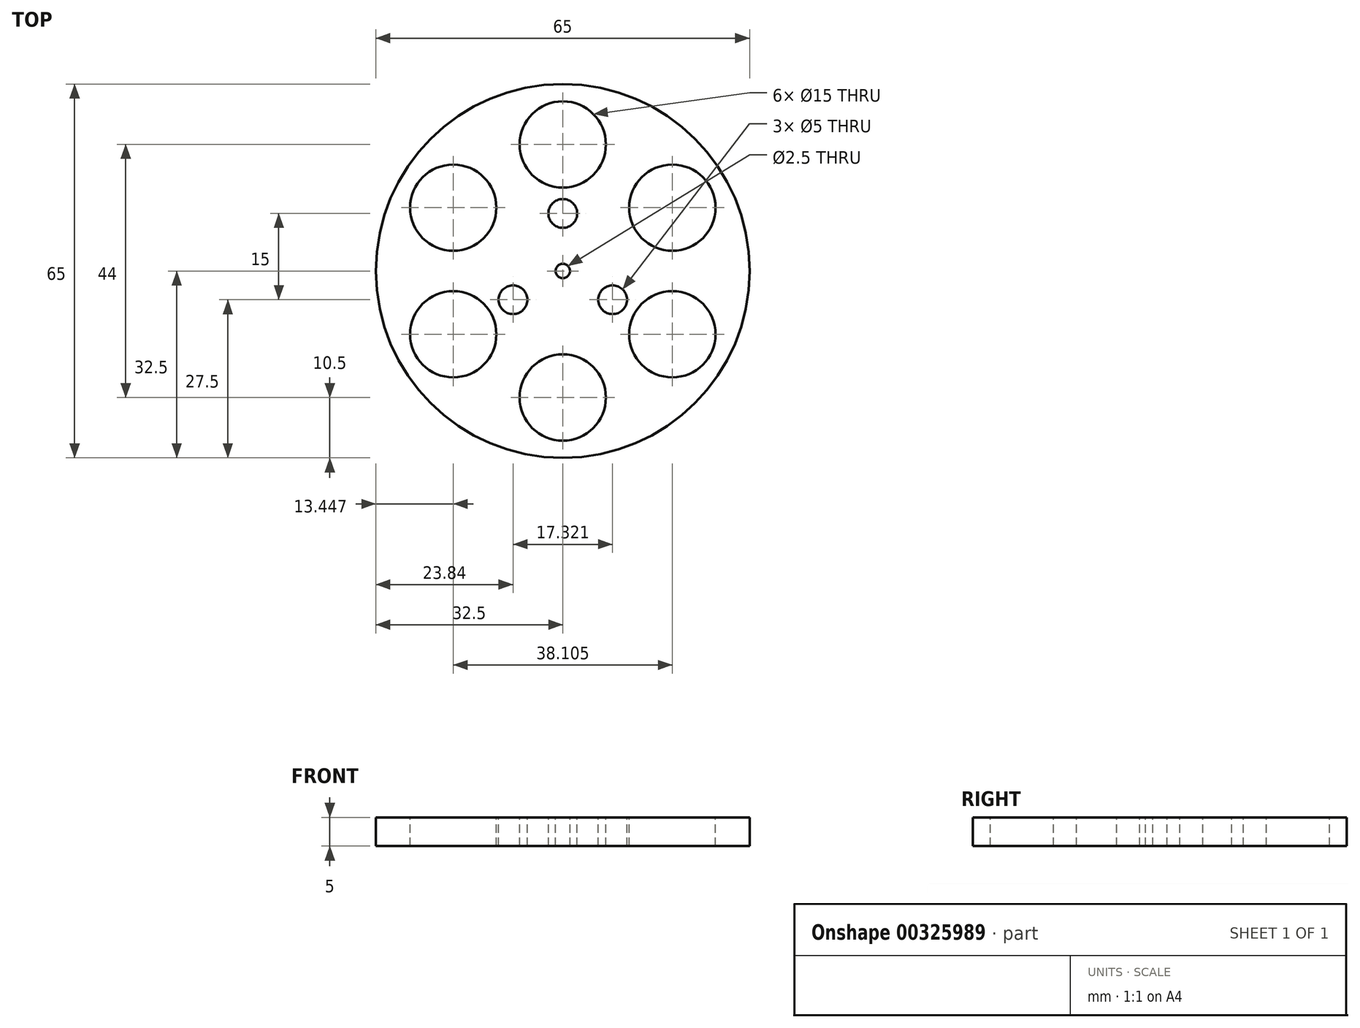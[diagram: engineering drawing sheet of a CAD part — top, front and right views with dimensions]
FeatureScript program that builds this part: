
annotation { "Feature Type Name" : "Feature", "Feature Type Description" : "" }
export const myFeature = defineFeature(function(context is Context, id is Id, definition is map)
    precondition{}
    {
        {
            var Q0;
            Q0=qCreatedBy(makeId("Top.planeOp"),FACE);
            var sketch = newSketch(context, id + "F0", { "sketchPlane" : qUnion([Q0])});
            skCircle(sketch, "E0", {"center": v(0, 0) * mm, "radius": 32.5 * mm});
            skLineSegment(sketch, "E1", {"start": v(0, 0) * mm, "end": v(0, 22) * mm});
            skLineSegment(sketch, "E2.1.0", {"start": v(0, 0) * mm, "end": v(19.05, 11) * mm});
            skLineSegment(sketch, "E2.2.0", {"start": v(0, 0) * mm, "end": v(19.05, -11) * mm});
            skLineSegment(sketch, "E2.3.0", {"start": v(0, 0) * mm, "end": v(0, -22) * mm});
            skLineSegment(sketch, "E2.4.0", {"start": v(0, 0) * mm, "end": v(-19.05, -11) * mm});
            skLineSegment(sketch, "E2.5.0", {"start": v(0, 0) * mm, "end": v(-19.05, 11) * mm});
            skLineSegment(sketch, "E2.anchor1", {"start": v(0, 0) * mm, "end": v(0, 22) * mm, "construction": true});
            skLineSegment(sketch, "E2.anchor2", {"start": v(0, 0) * mm, "end": v(-19.05, 11) * mm, "construction": true});
            skPoint(sketch, "E3", {"position": v(0, 10) * mm});
            skPoint(sketch, "E4.1.0", {"position": v(-8.66, -5) * mm});
            skPoint(sketch, "E4.2.0", {"position": v(8.66, -5) * mm});
            skSolve(sketch);
        }
        {
            var Q0;
            Q0=makeQuery(id+"F0.imprint","IMPRINT",FACE,{"disambiguationData":[TD([[makeQuery(id+"F0.imprint","IMPRINT",EDGE,{"derivedFrom":sQuery(id+"F0.wireOp",EDGE,"E0")}),1.0]])]});
            extrude(context, id + "F1", {"entities" : qUnion([Q0]), "depth" : 5 * mm, "offsetDistance" : 25 * mm});
        }
        {
            var Q0;
            Q0=sQuery(id+"F0.wireOp",VERTEX,"E2.1.0.end");
            var Q1;
            Q1=sQuery(id+"F0.wireOp",VERTEX,"E1.end");
            var Q2;
            Q2=sQuery(id+"F0.wireOp",VERTEX,"E2.5.0.end");
            var Q3;
            Q3=sQuery(id+"F0.wireOp",VERTEX,"E2.4.0.end");
            var Q4;
            Q4=sQuery(id+"F0.wireOp",VERTEX,"E2.3.0.end");
            var Q5;
            Q5=sQuery(id+"F0.wireOp",VERTEX,"E2.2.0.end");
            var Q6;
            Q6=makeQuery(id+"F1.opExtrude","SWEPT_BODY",BODY,{"disambiguationData":[OSD([sQuery(id+"F0.wireOp",EDGE,"E0")])]});
            hole(context, id + "F2", {"style" : HoleStyle.SIMPLE, "endStyle" : HoleEndStyle.THROUGH, "oppositeDirection" : true, "holeDiameter" : 15 * mm, "majorDiameter" : 5 * mm, "tappedDepth" : 12 * mm, "tapClearance" : 3, "locations" : qUnion([Q0, Q1, Q2, Q3, Q4, Q5]), "scope" : qUnion([Q6]), "startStyle" : HoleStartStyle.PART});
        }
        {
            var Q0;
            Q0=sQuery(id+"F0.wireOp",VERTEX,"E4.1.0");
            var Q1;
            Q1=sQuery(id+"F0.wireOp",VERTEX,"E3");
            var Q2;
            Q2=sQuery(id+"F0.wireOp",VERTEX,"E4.2.0");
            var Q3;
            Q3=makeQuery(id+"F1.opExtrude","SWEPT_BODY",BODY,{"disambiguationData":[OSD([sQuery(id+"F0.wireOp",EDGE,"E0")])]});
            hole(context, id + "F3", {"style" : HoleStyle.SIMPLE, "endStyle" : HoleEndStyle.THROUGH, "oppositeDirection" : true, "holeDiameter" : 5 * mm, "majorDiameter" : 5 * mm, "tappedDepth" : 12 * mm, "tapClearance" : 3, "locations" : qUnion([Q0, Q1, Q2]), "scope" : qUnion([Q3]), "startStyle" : HoleStartStyle.PART});
        }
        {
            var Q0;
            Q0=sQuery(id+"F0.wireOp",VERTEX,"E0.center");
            var Q1;
            Q1=makeQuery(id+"F1.opExtrude","SWEPT_BODY",BODY,{"disambiguationData":[OSD([sQuery(id+"F0.wireOp",EDGE,"E0")])]});
            hole(context, id + "F4", {"style" : HoleStyle.SIMPLE, "endStyle" : HoleEndStyle.BLIND, "oppositeDirection" : true, "holeDiameter" : 2.5 * mm, "majorDiameter" : 5 * mm, "holeDepth" : 10 * mm, "tappedDepth" : 12 * mm, "tapClearance" : 3, "locations" : qUnion([Q0]), "scope" : qUnion([Q1]), "startStyle" : HoleStartStyle.PART});
        }
    });
